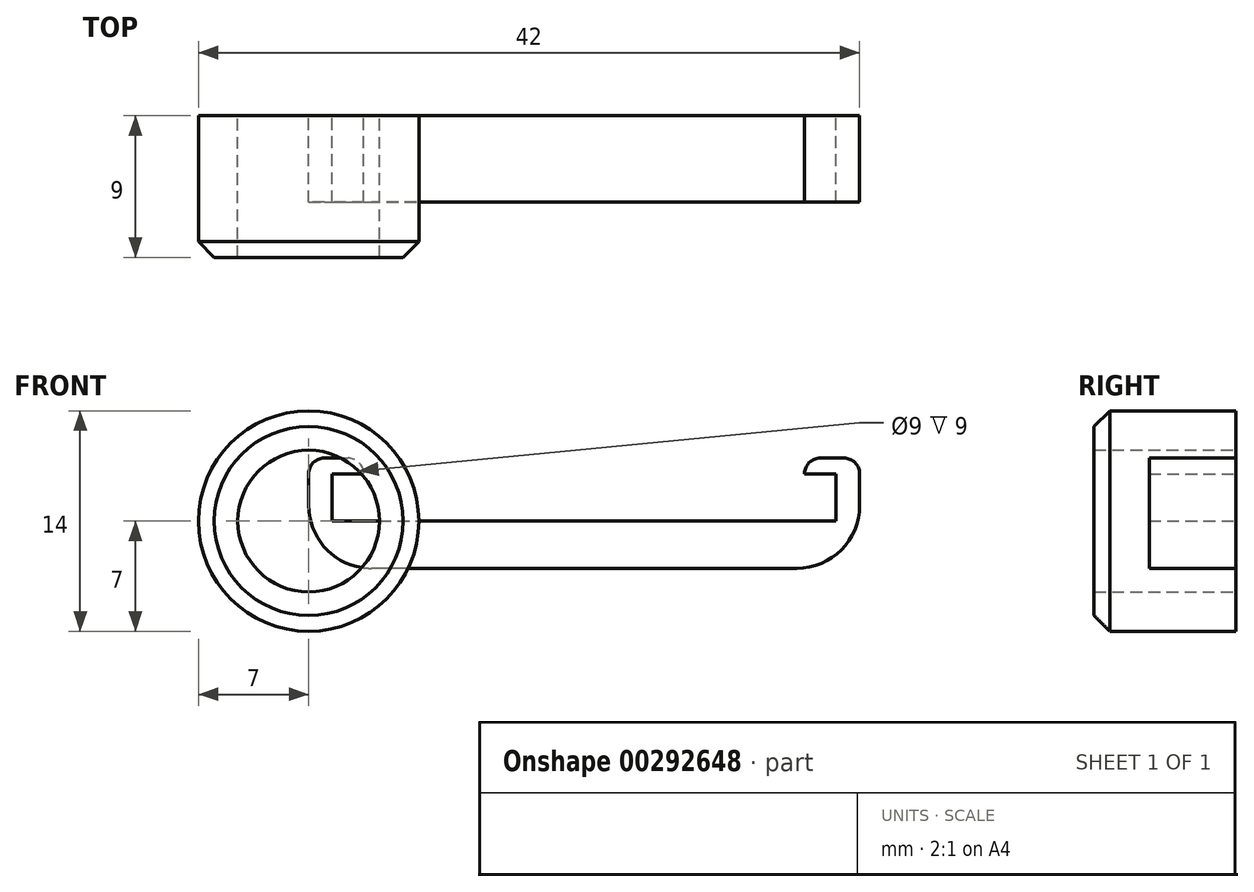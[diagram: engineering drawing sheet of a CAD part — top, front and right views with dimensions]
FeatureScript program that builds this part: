
annotation { "Feature Type Name" : "Feature", "Feature Type Description" : "" }
export const myFeature = defineFeature(function(context is Context, id is Id, definition is map)
    precondition{}
    {
        {
            var Q0;
            Q0=qCreatedBy(makeId("Front.planeOp"),FACE);
            var sketch = newSketch(context, id + "F0", { "sketchPlane" : qUnion([Q0])});
            skLineSegment(sketch, "E0", {"start": v(0, 0) * mm, "end": v(35, 0) * mm});
            skLineSegment(sketch, "E1", {"start": v(35, 0) * mm, "end": v(35, 4) * mm});
            skLineSegment(sketch, "E2", {"start": v(35, 4) * mm, "end": v(31.5, 4) * mm});
            skLineSegment(sketch, "E3", {"start": v(31.5, 4) * mm, "end": v(31.5, 3) * mm});
            skLineSegment(sketch, "E4", {"start": v(31.5, 3) * mm, "end": v(33.5, 3) * mm});
            skLineSegment(sketch, "E5", {"start": v(33.5, 3) * mm, "end": v(33.5, 0) * mm});
            skLineSegment(sketch, "E6", {"start": v(35, 0) * mm, "end": v(35, -3) * mm});
            skLineSegment(sketch, "E7", {"start": v(35, -3) * mm, "end": v(0, -3) * mm});
            skLineSegment(sketch, "E8", {"start": v(0, -3) * mm, "end": v(0, 0) * mm});
            skLineSegment(sketch, "E9", {"start": v(17.5, 0) * mm, "end": v(17.5, 2.64) * mm});
            skLineSegment(sketch, "E10.MirrorCS", {"start": v(1.5, 3) * mm, "end": v(1.5, 0) * mm});
            skLineSegment(sketch, "E11.MirrorCS", {"start": v(3.5, 3) * mm, "end": v(1.5, 3) * mm});
            skLineSegment(sketch, "E12.MirrorCS", {"start": v(3.5, 4) * mm, "end": v(3.5, 3) * mm});
            skLineSegment(sketch, "E13.MirrorCS", {"start": v(0, 0) * mm, "end": v(0, 4) * mm});
            skLineSegment(sketch, "E14.MirrorCS", {"start": v(0, 4) * mm, "end": v(3.5, 4) * mm});
            skSolve(sketch);
        }
        {
            var Q0;
            Q0 = qSketchRegion(id + "F0", true);
            extrude(context, id + "F1", {"entities" : qUnion([Q0]), "depth" : 5.5 * mm, "offsetDistance" : 25 * mm});
        }
        {
            var Q0;
            Q0=makeQuery(id+"F1.opExtrude","SWEPT_EDGE",EDGE,{"disambiguationData":[OSD([sQuery(id+"F0.wireOp",EDGE,"E2"),sQuery(id+"F0.wireOp",EDGE,"E3")])]});
            var Q1;
            Q1=makeQuery(id+"F1.opExtrude","SWEPT_EDGE",EDGE,{"disambiguationData":[OSD([sQuery(id+"F0.wireOp",EDGE,"E12.MirrorCS"),sQuery(id+"F0.wireOp",EDGE,"E14.MirrorCS")])]});
            var Q2;
            Q2=makeQuery(id+"F1.opExtrude","SWEPT_EDGE",EDGE,{"disambiguationData":[OSD([sQuery(id+"F0.wireOp",EDGE,"E1"),sQuery(id+"F0.wireOp",EDGE,"E2")])]});
            var Q3;
            Q3=makeQuery(id+"F1.opExtrude","SWEPT_EDGE",EDGE,{"disambiguationData":[OSD([sQuery(id+"F0.wireOp",EDGE,"E13.MirrorCS"),sQuery(id+"F0.wireOp",EDGE,"E14.MirrorCS")])]});
            fillet(context, id + "F2", {"entities" : qUnion([Q0, Q1, Q2, Q3]), "tangentPropagation" : true, "radius" : 1 * mm, "defaultsChanged" : false, "vertexSettings" : [], "allowEdgeOverflow" : false});
        }
        {
            var Q0;
            Q0=makeQuery(id+"F1.opExtrude","SWEPT_EDGE",EDGE,{"disambiguationData":[OSD([sQuery(id+"F0.wireOp",EDGE,"E7"),sQuery(id+"F0.wireOp",EDGE,"E8")])]});
            var Q1;
            Q1=makeQuery(id+"F1.opExtrude","SWEPT_EDGE",EDGE,{"disambiguationData":[OSD([sQuery(id+"F0.wireOp",EDGE,"E6"),sQuery(id+"F0.wireOp",EDGE,"E7")])]});
            fillet(context, id + "F3", {"entities" : qUnion([Q0, Q1]), "tangentPropagation" : true, "radius" : 4 * mm, "defaultsChanged" : true, "vertexSettings" : [], "allowEdgeOverflow" : false});
        }
        {
            var Q0;
            Q0=qCreatedBy(makeId("Front.planeOp"),FACE);
            var sketch = newSketch(context, id + "F4", { "sketchPlane" : qUnion([Q0])});
            skCircle(sketch, "E15", {"center": v(0, 0) * mm, "radius": 4.5 * mm});
            skCircle(sketch, "E16", {"center": v(0, 0) * mm, "radius": 7 * mm});
            skSolve(sketch);
        }
        {
            var Q0;
            Q0=makeQuery(id+"F4.imprint","IMPRINT",FACE,{"disambiguationData":[TD([[makeQuery(id+"F4.imprint","IMPRINT",EDGE,{"derivedFrom":sQuery(id+"F4.wireOp",EDGE,"E15")}),-1.0]])]});
            extrude(context, id + "F5", {"entities" : qUnion([Q0]), "depth" : 9 * mm, "offsetDistance" : 25 * mm});
        }
        {
            var Q0;
            Q0=makeQuery(id+"F5.opExtrude","CAP_EDGE",EDGE,{"disambiguationData":[OSD([sQuery(id+"F4.wireOp",EDGE,"E16")])],"isStart":false});
            chamfer(context, id + "F6", {"entities" : qUnion([Q0]), "width" : 1 * mm, "tangentPropagation" : true});
        }
    });
